# Revit family: Notes-LivingDivani
name_source: partatom
category: Furniture
revit_build: Autodesk Revit 2014 (Build: 20130308_1515(x64)
units: mm (PartAtom-declared; Revit-internal decimal feet)

## types (6) — shared parameters
Manufacturer = LivingDivani
Mat. Gambe = Zinc
Mat. Tavolo = Zinc
Mat. pietra = Stone
Mat. vetro = Glass, Clear Glazing, Tempered
Model = Notes
URL = http://www.livingdivani.it

## per-type parameters (varying)
| type | Codice prodotto | Raggio tavolo | Tavolo grande | Tavolo grande o piccolo | Tavolo piccolo | Tavolo pietra | Tavolo vetro | Tavolo vetro o pietra |
| Tav.Pietra 140cm | NOTV140 | 70 cm | No | No | No | Yes | No | Yes |
| Tav. Vetro 140cm | NOTV140 | 70 cm | No | No | No | No | Yes | No |
| Tav. Vetro 160cm | NOTV160 | 80 cm | No | Yes | Yes | No | Yes | No |
| Tav. Pietra 160cm | NOTV160 | 80 cm | No | Yes | Yes | Yes | No | Yes |
| Tav. Pietra 180cm | NOTV180 | 90 cm | Yes | Yes | No | Yes | No | Yes |
| Tav. Vetro 180cm | NOTV180 | 90 cm | Yes | Yes | No | No | Yes | No |
